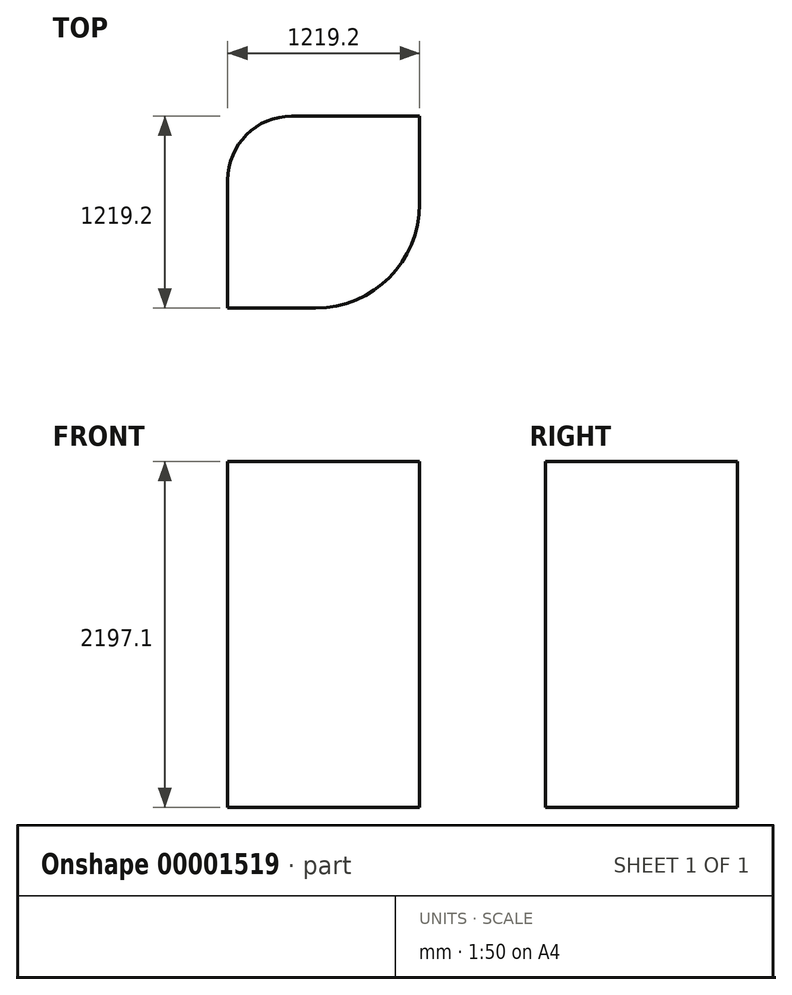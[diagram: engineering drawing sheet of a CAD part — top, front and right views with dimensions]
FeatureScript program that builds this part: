
annotation { "Feature Type Name" : "Feature", "Feature Type Description" : "" }
export const myFeature = defineFeature(function(context is Context, id is Id, definition is map)
    precondition{}
    {
        {
            var Q0;
            Q0=qCreatedBy(makeId("Top.planeOp"),FACE);
            var sketch = newSketch(context, id + "F0", { "sketchPlane" : qUnion([Q0])});
            skLineSegment(sketch, "E0.bottom", {"start": v(406.4, 0) * mm, "end": v(1219.2, 0) * mm});
            skLineSegment(sketch, "E0.top", {"start": v(0, -1219.2) * mm, "end": v(558.8, -1219.2) * mm});
            skLineSegment(sketch, "E0.left", {"start": v(0, -406.4) * mm, "end": v(0, -1219.2) * mm});
            skLineSegment(sketch, "E0.right", {"start": v(1219.2, 0) * mm, "end": v(1219.2, -558.8) * mm});
            skPoint(sketch, "E1.visualSharp", {"position": v(0, 0) * mm});
            skArc(sketch, "E1.filletArc", {"start": v(406.4, 0) * mm, "mid": v(119.03, -119.03) * mm, "end": v(0, -406.4) * mm});
            skPoint(sketch, "E2.visualSharp", {"position": v(1219.2, -1219.2) * mm});
            skArc(sketch, "E2.filletArc", {"start": v(558.8, -1219.2) * mm, "mid": v(1025.77, -1025.77) * mm, "end": v(1219.2, -558.8) * mm});
            skSolve(sketch);
        }
        {
            var Q0;
            Q0=makeQuery(id+"F0.imprint","IMPRINT",FACE,{"disambiguationData":[TD([[makeQuery(id+"F0.imprint","IMPRINT",EDGE,{"derivedFrom":sQuery(id+"F0.wireOp",EDGE,"E0.bottom")}),-1.0]])]});
            extrude(context, id + "F1", {"entities" : qUnion([Q0]), "depth" : 2197.1 * mm});
        }
    });
